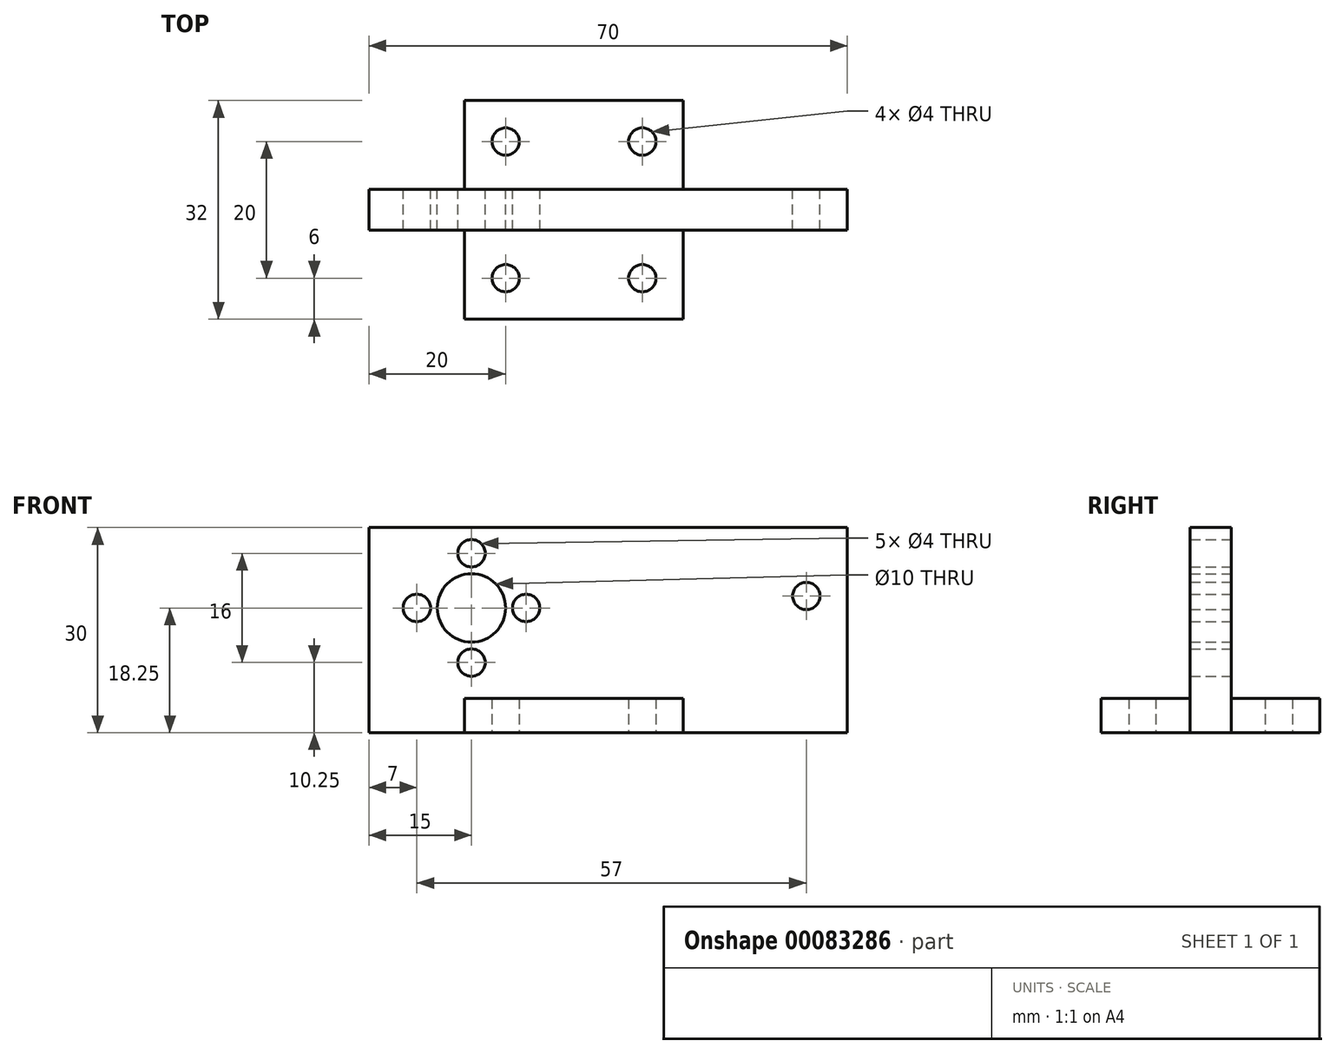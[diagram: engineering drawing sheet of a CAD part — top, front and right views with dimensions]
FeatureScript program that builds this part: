
annotation { "Feature Type Name" : "Feature", "Feature Type Description" : "" }
export const myFeature = defineFeature(function(context is Context, id is Id, definition is map)
    precondition{}
    {
        {
            var Q0;
            Q0=qCreatedBy(makeId("Top.planeOp"),FACE);
            var sketch = newSketch(context, id + "F0", { "sketchPlane" : qUnion([Q0])});
            skLineSegment(sketch, "E0.bottom", {"start": v(16, 16) * mm, "end": v(-16, 16) * mm});
            skLineSegment(sketch, "E0.top", {"start": v(16, -16) * mm, "end": v(-16, -16) * mm});
            skLineSegment(sketch, "E0.left", {"start": v(16, 16) * mm, "end": v(16, -16) * mm});
            skLineSegment(sketch, "E0.right", {"start": v(-16, 16) * mm, "end": v(-16, -16) * mm});
            skPoint(sketch, "E0.middle", {"position": v(0, 0) * mm});
            skLineSegment(sketch, "E1.bottom", {"start": v(10, 10) * mm, "end": v(-10, 10) * mm, "construction": true});
            skLineSegment(sketch, "E1.top", {"start": v(10, -10) * mm, "end": v(-10, -10) * mm, "construction": true});
            skLineSegment(sketch, "E1.left", {"start": v(10, 10) * mm, "end": v(10, -10) * mm, "construction": true});
            skLineSegment(sketch, "E1.right", {"start": v(-10, 10) * mm, "end": v(-10, -10) * mm, "construction": true});
            skCircle(sketch, "E2", {"center": v(-10, 10) * mm, "radius": 2 * mm});
            skCircle(sketch, "E3", {"center": v(10, 10) * mm, "radius": 2 * mm});
            skCircle(sketch, "E4", {"center": v(10, -10) * mm, "radius": 2 * mm});
            skCircle(sketch, "E5", {"center": v(-10, -10) * mm, "radius": 2 * mm});
            skSolve(sketch);
        }
        {
            var Q0;
            Q0 = qSketchRegion(id + "F0", true);
            extrude(context, id + "F1", {"entities" : qUnion([Q0]), "depth" : 5 * mm, "offsetDistance" : 25 * mm});
        }
        {
            var Q0;
            Q0=qCreatedBy(makeId("Front.planeOp"),FACE);
            var sketch = newSketch(context, id + "F2", { "sketchPlane" : qUnion([Q0])});
            skLineSegment(sketch, "E6.bottom", {"start": v(40, 0) * mm, "end": v(-30, 0) * mm});
            skLineSegment(sketch, "E6.top", {"start": v(40, 30) * mm, "end": v(-30, 30) * mm});
            skLineSegment(sketch, "E6.left", {"start": v(40, 0) * mm, "end": v(40, 30) * mm});
            skLineSegment(sketch, "E6.right", {"start": v(-30, 0) * mm, "end": v(-30, 30) * mm});
            skCircle(sketch, "E7", {"center": v(-15, 18.25) * mm, "radius": 5 * mm});
            skLineSegment(sketch, "E8", {"start": v(-34.68, -12.75) * mm, "end": v(14.18, -12.75) * mm, "construction": true});
            skCircle(sketch, "E9", {"center": v(-15, 18.25) * mm, "radius": 8 * mm, "construction": true});
            skCircle(sketch, "E10", {"center": v(-23, 18.25) * mm, "radius": 2 * mm});
            skCircle(sketch, "E11.1.0", {"center": v(-15, 10.25) * mm, "radius": 2 * mm});
            skCircle(sketch, "E11.2.0", {"center": v(-7, 18.25) * mm, "radius": 2 * mm});
            skCircle(sketch, "E11.3.0", {"center": v(-15, 26.25) * mm, "radius": 2 * mm});
            skCircle(sketch, "E12", {"center": v(34, 20) * mm, "radius": 2 * mm});
            skSolve(sketch);
        }
        {
            var Q0;
            Q0 = qSketchRegion(id + "F2", true);
            extrude(context, id + "F3", {"entities" : qUnion([Q0]), "operationType" : NewBodyOperationType.ADD, "endBound" : BoundingType.SYMMETRIC, "depth" : 6 * mm, "offsetDistance" : 25 * mm});
        }
    });
